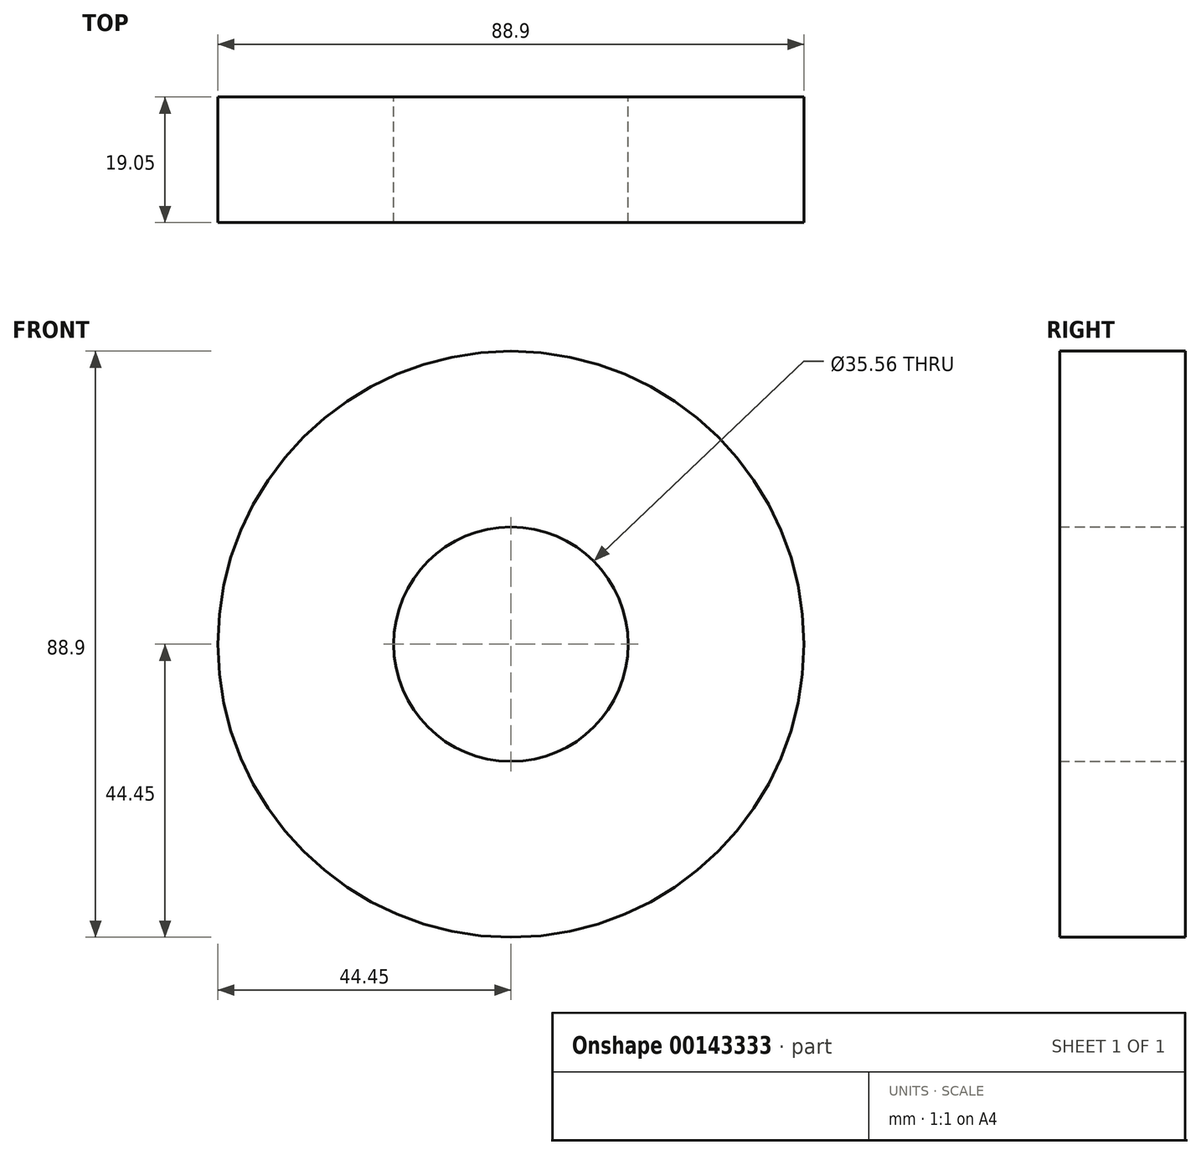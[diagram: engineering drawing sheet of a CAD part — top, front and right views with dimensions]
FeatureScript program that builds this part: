
annotation { "Feature Type Name" : "Feature", "Feature Type Description" : "" }
export const myFeature = defineFeature(function(context is Context, id is Id, definition is map)
    precondition{}
    {
        {
            var Q0;
            Q0=qCreatedBy(makeId("Front.planeOp"),FACE);
            var sketch = newSketch(context, id + "F0", { "sketchPlane" : qUnion([Q0])});
            skCircle(sketch, "E0", {"center": v(0, 0) * mm, "radius": 17.78 * mm});
            skCircle(sketch, "E1", {"center": v(0, 0) * mm, "radius": 44.45 * mm});
            skSolve(sketch);
        }
        {
            var Q0;
            Q0 = qSketchRegion(id + "F0", true);
            extrude(context, id + "F1", {"entities" : qUnion([Q0]), "depth" : 19.05 * mm});
        }
    });
